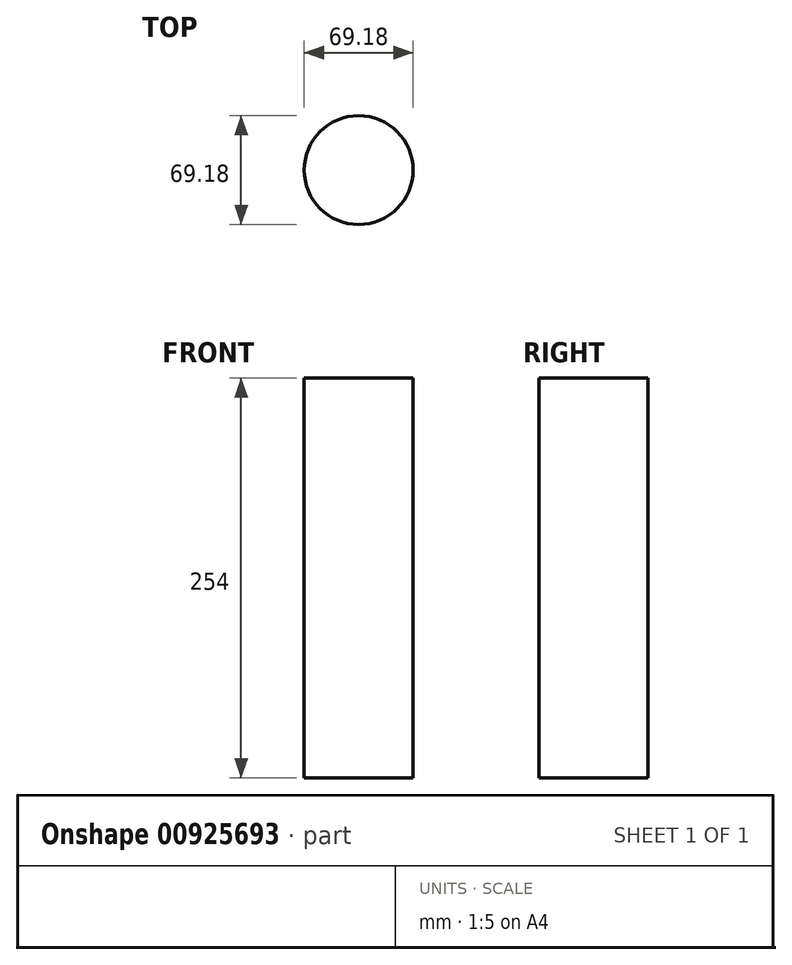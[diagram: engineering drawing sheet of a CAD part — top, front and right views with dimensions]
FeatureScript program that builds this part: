
annotation { "Feature Type Name" : "Feature", "Feature Type Description" : "" }
export const myFeature = defineFeature(function(context is Context, id is Id, definition is map)
    precondition{}
    {
        {
            var Q0;
            Q0=qCreatedBy(makeId("Top.planeOp"),FACE);
            var sketch = newSketch(context, id + "F0", { "sketchPlane" : qUnion([Q0])});
            skCircle(sketch, "E0", {"center": v(0, 0) * mm, "radius": 34.59 * mm});
            skSolve(sketch);
        }
        {
            var Q0;
            Q0 = qSketchRegion(id + "F0", true);
            extrude(context, id + "F1", {"entities" : qUnion([Q0]), "depth" : 254 * mm, "offsetDistance" : 25.4 * mm});
        }
    });
